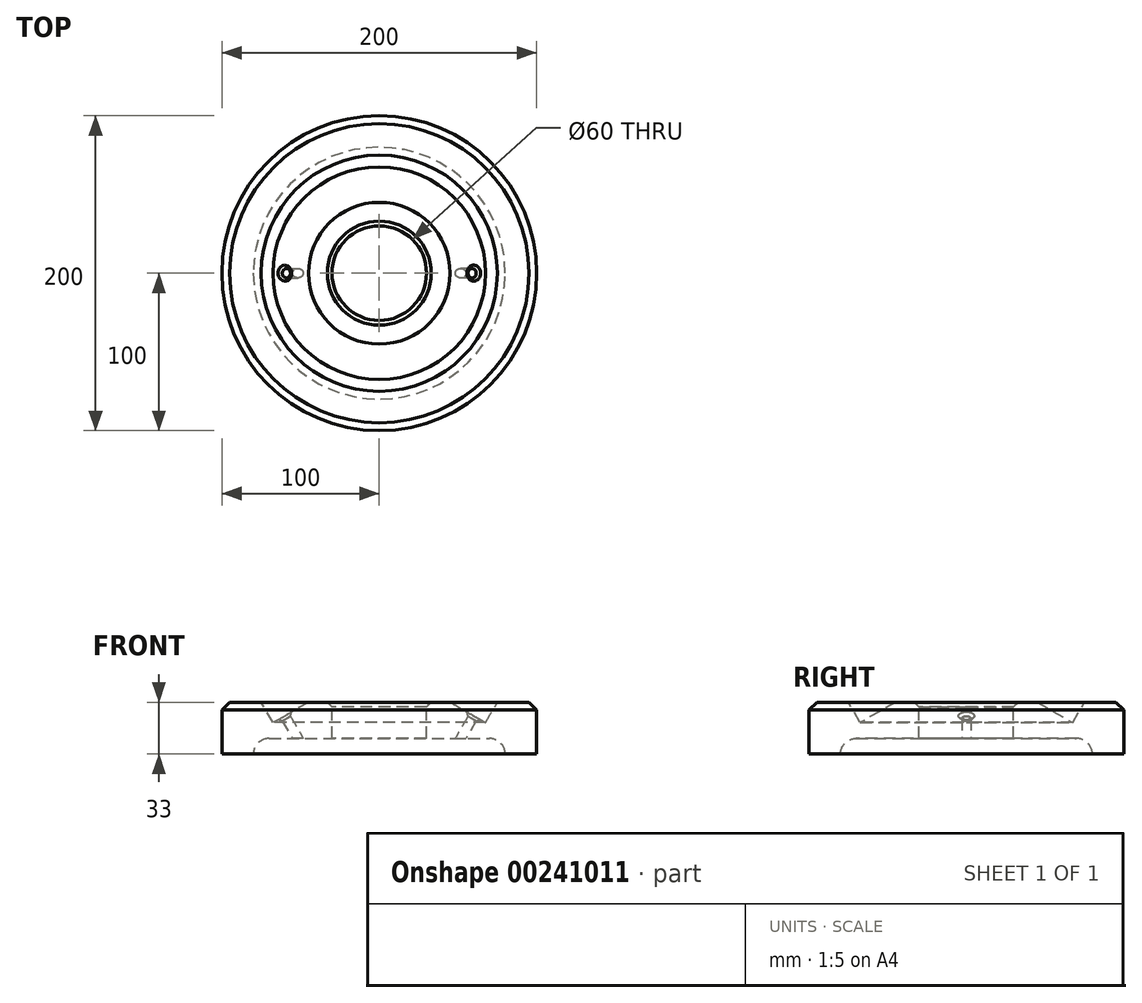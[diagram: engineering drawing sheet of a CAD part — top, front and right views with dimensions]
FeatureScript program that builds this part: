
annotation { "Feature Type Name" : "Feature", "Feature Type Description" : "" }
export const myFeature = defineFeature(function(context is Context, id is Id, definition is map)
    precondition{}
    {
        {
            var Q0;
            Q0=qCreatedBy(makeId("Front.planeOp"),FACE);
            var sketch = newSketch(context, id + "F0", { "sketchPlane" : qUnion([Q0])});
            skLineSegment(sketch, "E0", {"start": v(30, 10) * mm, "end": v(30, 33) * mm});
            skLineSegment(sketch, "E1", {"start": v(30, 33) * mm, "end": v(44.98, 33) * mm});
            skLineSegment(sketch, "E2", {"start": v(44.98, 33) * mm, "end": v(67.5, 20) * mm});
            skLineSegment(sketch, "E3", {"start": v(67.5, 20) * mm, "end": v(75, 33) * mm});
            skLineSegment(sketch, "E4", {"start": v(75, 33) * mm, "end": v(100, 33) * mm});
            skLineSegment(sketch, "E5", {"start": v(100, 33) * mm, "end": v(100, 0) * mm});
            skLineSegment(sketch, "E6", {"start": v(100, 0) * mm, "end": v(80, 0) * mm});
            skLineSegment(sketch, "E7", {"start": v(80, 0) * mm, "end": v(80, 10) * mm});
            skLineSegment(sketch, "E8", {"start": v(80, 10) * mm, "end": v(30, 10) * mm});
            skLineSegment(sketch, "E9", {"start": v(0, 81.27) * mm, "end": v(0, -23.1) * mm, "construction": true});
            skSolve(sketch);
        }
        {
            var Q0;
            Q0=makeQuery(id+"F0.imprint","IMPRINT",FACE,{"disambiguationData":[TD([[makeQuery(id+"F0.imprint","IMPRINT",EDGE,{"derivedFrom":sQuery(id+"F0.wireOp",EDGE,"E0")}),-1.0]])]});
            var Q1;
            Q1=sQuery(id+"F0.wireOp",EDGE,"E9");
            revolve(context, id + "F1", {"entities" : qUnion([Q0]), "axis" : qUnion([Q1]), "revolveType" : RevolveType.FULL});
        }
        {
            var Q0;
            Q0=qCreatedBy(makeId("Front.planeOp"),FACE);
            var sketch = newSketch(context, id + "F2", { "sketchPlane" : qUnion([Q0])});
            skLineSegment(sketch, "E10", {"start": v(44.98, 33) * mm, "end": v(67.5, 20) * mm, "construction": true});
            skLineSegment(sketch, "E11", {"start": v(67.5, 20) * mm, "end": v(75, 33) * mm, "construction": true});
            skLineSegment(sketch, "E12", {"start": v(67.6, 37.5) * mm, "end": v(38.92, -12.2) * mm, "construction": true});
            skPoint(sketch, "E13", {"position": v(60, 24.34) * mm});
            skLineSegment(sketch, "E14.0", {"start": v(64.42, 38) * mm, "end": v(40.48, -3.5) * mm});
            skLineSegment(sketch, "E15", {"start": v(67.02, 36.5) * mm, "end": v(64.42, 38) * mm});
            skLineSegment(sketch, "E16", {"start": v(43.08, -5) * mm, "end": v(40.48, -3.5) * mm});
            skLineSegment(sketch, "E17", {"start": v(43.08, -5) * mm, "end": v(67.02, 36.5) * mm});
            skSolve(sketch);
        }
        {
            var Q0;
            Q0=makeQuery(id+"F2.imprint","IMPRINT",FACE,{"disambiguationData":[TD([[makeQuery(id+"F2.imprint","IMPRINT",EDGE,{"derivedFrom":sQuery(id+"F2.wireOp",EDGE,"E14.0")}),1.0]])]});
            var Q1;
            Q1=sQuery(id+"F2.wireOp",EDGE,"E12");
            revolve(context, id + "F3", {"operationType" : NewBodyOperationType.REMOVE, "entities" : qUnion([Q0]), "axis" : qUnion([Q1]), "revolveType" : RevolveType.FULL, "oppositeDirection" : true});
        }
        {
            var Q0;
            Q0=makeQuery(id+"F3.boolean.opBoolean","COPY",FACE,{"derivedFrom":makeQuery(id+"F3.opRevolve","SWEPT_FACE",FACE,{"disambiguationData":[OSD([sQuery(id+"F2.wireOp",EDGE,"E14.0")])]})});
            var Q1;
            Q1=sQuery(id+"F0.wireOp",EDGE,"E9");
            circularPattern(context, id + "F4", {"patternType" : PatternType.FACE, "faces" : qUnion([Q0]), "axis" : qUnion([Q1]), "angle" : 360 * degree, "instanceCount" : 2, "equalSpace" : true});
        }
        {
            var Q0;
            Q0=makeQuery(id+"F3.boolean.opBoolean","INTERSECT",EDGE,{"derivedFrom":[makeQuery(id+"F1.opRevolve","SWEPT_FACE",FACE,{"disambiguationData":[OSD([sQuery(id+"F0.wireOp",EDGE,"E2")])]}),makeQuery(id+"F3.opRevolve","SWEPT_FACE",FACE,{"disambiguationData":[OSD([sQuery(id+"F2.wireOp",EDGE,"E14.0")])]})]});
            var Q1;
            Q1=makeQuery(id+"F4.opPattern","COPY",EDGE,{"derivedFrom":makeQuery(id+"F3.boolean.opBoolean","INTERSECT",EDGE,{"derivedFrom":[makeQuery(id+"F1.opRevolve","SWEPT_FACE",FACE,{"disambiguationData":[OSD([sQuery(id+"F0.wireOp",EDGE,"E2")])]}),makeQuery(id+"F3.opRevolve","SWEPT_FACE",FACE,{"disambiguationData":[OSD([sQuery(id+"F2.wireOp",EDGE,"E14.0")])]})]}),"instanceName":"1"});
            chamfer(context, id + "F5", {"entities" : qUnion([Q0, Q1]), "width" : 2 * mm, "tangentPropagation" : true});
        }
        {
            var Q0;
            Q0=makeQuery(id+"F1.opRevolve","SWEPT_EDGE",EDGE,{"disambiguationData":[OSD([sQuery(id+"F0.wireOp",EDGE,"E0"),sQuery(id+"F0.wireOp",EDGE,"E1")])]});
            chamfer(context, id + "F6", {"entities" : qUnion([Q0]), "width" : 3 * mm, "tangentPropagation" : true});
        }
        {
            var Q0;
            Q0=makeQuery(id+"F1.opRevolve","SWEPT_EDGE",EDGE,{"disambiguationData":[OSD([sQuery(id+"F0.wireOp",EDGE,"E4"),sQuery(id+"F0.wireOp",EDGE,"E5")])]});
            chamfer(context, id + "F7", {"entities" : qUnion([Q0]), "width" : 5 * mm, "tangentPropagation" : true});
        }
        {
            var Q0;
            Q0=makeQuery(id+"F1.opRevolve","SWEPT_EDGE",EDGE,{"disambiguationData":[OSD([sQuery(id+"F0.wireOp",EDGE,"E7"),sQuery(id+"F0.wireOp",EDGE,"E8")])]});
            fillet(context, id + "F8", {"entities" : qUnion([Q0]), "radius" : 10 * mm, "tangentPropagation" : true, "allowEdgeOverflow" : false});
        }
    });
